# Revit family: CPFD_CW_UBD
name_source: partatom
category: Mechanical Equipment
units: mm (PartAtom-declared; Revit-internal decimal feet)

## family parameters
Always vertical = Yes
Cut with Voids When Loaded = No
Part Type = Normal
Room Calculation Point = No
Round Connector Dimension = Use Radius
Shared = No
Work Plane-Based = No

## types (5) — shared parameters
0 = 0' - 0"
1" = 0' - 1"
1.5 = 0' - 1 1/2"
2" = 0' - 2"
2' = 2' - 0"
3" = 0' - 3"
4" = 0' - 4"
K = 0' - 1"
Manufacturer = Loren Cook Company
Model = CPFD_CW_UBD
ONE EIGTH = 0' - 0 1/8"
T_SQ = 2' - 8"
T_SQ/2 = 1' - 4"
Type Comments = Forward Curved Centrifugal Blower Direct Drive Clockwise Up Blast Arrangement 4
URL = www.lorencook.com

## per-type parameters (varying)
- 6_CPFD_CW_UBD: (P/2)-.125"=0' - 3 3/8"; A=1' - 1 1/2"; A/2=0' - 6 3/4"; B=1' - 6 1/2"; B-F-.25"=1' - 1 5/8"; B-F-2"=0' - 11 7/8"; B/2=0' - 9 1/4"; C=1' - 1 7/8"; C/2=0' - 6 15/16"; D=0' - 8 1/8"; E=0' - 7 7/8"; E+.25"=0' - 8 1/8"; F=0' - 4 5/8"; F+.25"=-0' - 4 7/8"; F+1.25"=-0' - 5 7/8"; G=0' - 5 3/4"; G-1"=0' - 4 3/4"; H=1' - 0 1/2"; H-1.5"=0' - 11"; H/2=0' - 6 1/4"; J=0' - 10 3/4"; L=0' - 4 5/8"; M=0' - 3 5/8"; N=0' - 0 7/16"; N/2=0' - 0 7/32"; P=0' - 7"; P/2=0' - 3 1/2"; P/6=0' - 1 5/32"; Q=0' - 0 1/2"; SPACE=0' - 1 1/2"
- 7_CPFD_CW_UBD: (P/2)-.125"=0' - 3 3/8"; A=1' - 1 1/2"; A/2=0' - 6 3/4"; B=1' - 8 1/4"; B-F-.25"=1' - 2 5/8"; B-F-2"=1' - 0 7/8"; B/2=0' - 10 1/8"; C=1' - 4 3/4"; C/2=0' - 8 3/8"; D=0' - 10 1/8"; E=0' - 8 3/8"; E+.25"=0' - 8 5/8"; F=0' - 5 3/8"; F+.25"=-0' - 5 5/8"; F+1.25"=-0' - 6 5/8"; G=0' - 6 1/8"; G-1"=0' - 5 1/8"; H=1' - 0 1/2"; H-1.5"=0' - 11"; H/2=0' - 6 1/4"; J=1' - 0 1/4"; L=0' - 7 1/8"; M=0' - 3 5/8"; N=0' - 0 7/16"; N/2=0' - 0 7/32"; P=0' - 7"; P/2=0' - 3 1/2"; P/6=0' - 1 5/32"; Q=0' - 0 5/8"; SPACE=0' - 1 1/2"
- 9_CPFD_CW_UBD: (P/2)-.125"=0' - 4 3/8"; A=1' - 2"; A/2=0' - 7"; B=1' - 9 3/4"; B-F-.25"=1' - 3 5/8"; B-F-2"=1' - 1 7/8"; B/2=0' - 10 7/8"; C=1' - 6 1/8"; C/2=0' - 9 1/16"; D=0' - 11 1/8"; E=0' - 9 7/8"; E+.25"=0' - 10 1/8"; F=0' - 5 7/8"; F+.25"=-0' - 6 1/8"; F+1.25"=-0' - 7 1/8"; G=0' - 7"; G-1"=0' - 6"; H=1' - 0 3/4"; H-1.5"=0' - 11 1/4"; H/2=0' - 6 3/8"; J=1' - 1 3/4"; L=0' - 7 5/8"; M=0' - 4 5/8"; N=0' - 0 9/16"; N/2=0' - 0 9/32"; P=0' - 9"; P/2=0' - 4 1/2"; P/6=0' - 1 1/2"; Q=0' - 0 3/4"; SPACE=0' - 2"
- 10_CPFD_CW_UBD: (P/2)-.125"=0' - 4 3/8"; A=1' - 3 1/2"; A/2=0' - 7 3/4"; B=1' - 10 1/4"; B-F-.25"=1' - 3 5/8"; B-F-2"=1' - 1 7/8"; B/2=0' - 11 1/8"; C=1' - 10 3/8"; C/2=0' - 11 3/16"; D=1' - 2 3/8"; E=0' - 11 3/8"; E+.25"=0' - 11 5/8"; F=0' - 6 3/8"; F+.25"=-0' - 6 5/8"; F+1.25"=-0' - 7 5/8"; G=0' - 8"; G-1"=0' - 7"; H=1' - 2 1/4"; H-1.5"=1' - 0 3/4"; H/2=0' - 7 1/8"; J=1' - 1 3/4"; L=0' - 9 7/8"; M=0' - 4 5/8"; N=0' - 0 9/16"; N/2=0' - 0 9/32"; P=0' - 9"; P/2=0' - 4 1/2"; P/6=0' - 1 1/2"; Q=0' - 1 1/16"; SPACE=0' - 1 1/2"
- 12_CPFD_CW_UBD: (P/2)-.125"=0' - 6 1/8"; A=1' - 5"; A/2=0' - 8 1/2"; B=1' - 10 3/4"; B-F-.25"=1' - 4 5/8"; B-F-2"=1' - 2 7/8"; B/2=0' - 11 3/8"; C=1' - 10 3/8"; C/2=0' - 11 3/16"; D=1' - 2 3/8"; E=1' - 1 3/8"; E+.25"=1' - 1 5/8"; F=0' - 5 7/8"; F+.25"=-0' - 6 1/8"; F+1.25"=-0' - 7 1/8"; G=0' - 9"; G-1"=0' - 8"; H=1' - 3 3/4"; H-1.5"=1' - 2 1/4"; H/2=0' - 7 7/8"; J=1' - 2 1/4"; L=0' - 9 7/8"; M=0' - 4 5/8"; N=0' - 0 9/16"; N/2=0' - 0 9/32"; P=1' - 0 1/2"; P/2=0' - 6 1/4"; P/6=0' - 2 3/32"; Q=0' - 1"; SPACE=0' - 2 1/2"

## geometry (parser evidence)
native form markers: Sweep x2
no freeform markers — native parametric forms only
